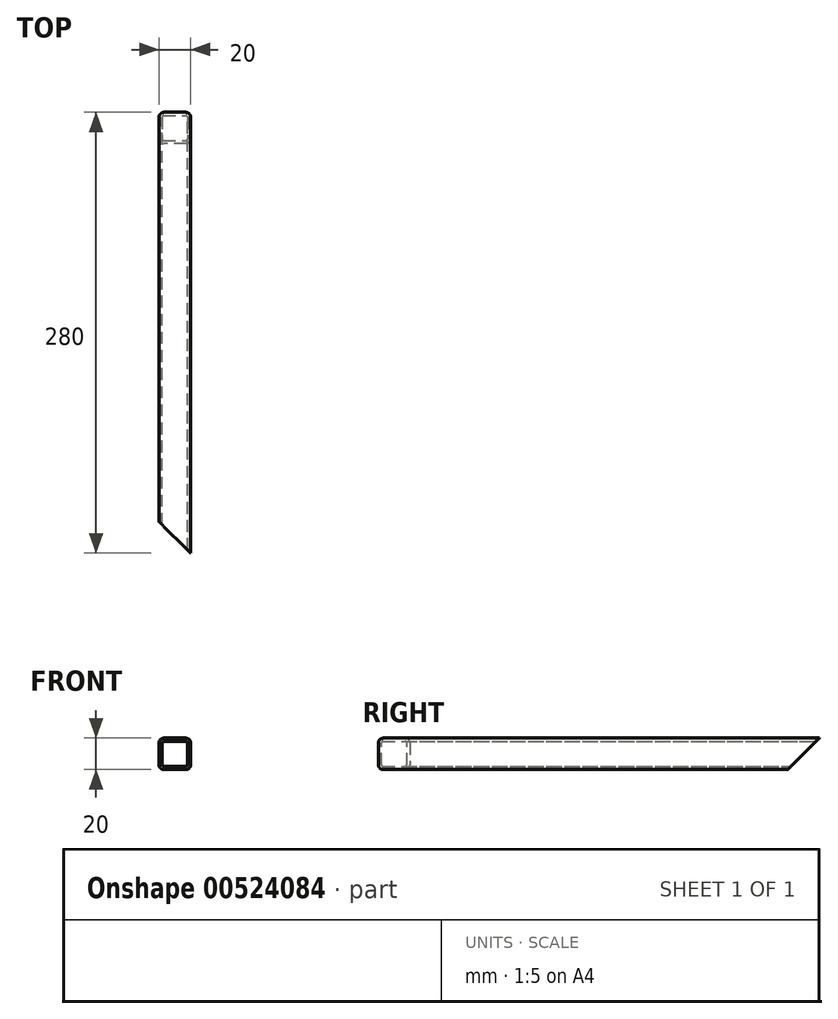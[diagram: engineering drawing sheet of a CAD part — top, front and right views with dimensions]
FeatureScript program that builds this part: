
annotation { "Feature Type Name" : "Feature", "Feature Type Description" : "" }
export const myFeature = defineFeature(function(context is Context, id is Id, definition is map)
    precondition{}
    {
        {
            assignVariable(context, id + "F0", {"name" : "R", "anyValue" : 3});
        }
        {
            assignVariable(context, id + "F1", {"name" : "W", "anyValue" : 2});
        }
        {
            var Q0;
            Q0=qCreatedBy(makeId("Front.planeOp"),FACE);
            var sketch = newSketch(context, id + "F2", { "sketchPlane" : qUnion([Q0])});
            skLineSegment(sketch, "E0.bottom", {"start": v(-10, 10) * mm, "end": v(10, 10) * mm});
            skLineSegment(sketch, "E0.top", {"start": v(-10, -10) * mm, "end": v(10, -10) * mm});
            skLineSegment(sketch, "E0.left", {"start": v(-10, 10) * mm, "end": v(-10, -10) * mm});
            skLineSegment(sketch, "E0.right", {"start": v(10, 10) * mm, "end": v(10, -10) * mm});
            skSolve(sketch);
        }
        {
            var Q0;
            Q0=qSketchRegion(id+"F2",true);
            extrude(context, id + "F3", {"entities" : qUnion([Q0]), "endBound" : BoundingType.SYMMETRIC, "depth" : 280 * mm, "offsetDistance" : 25 * mm});
        }
        {
            var Q0;
            Q0=makeQuery(id+"F3.opExtrude","SWEPT_EDGE",EDGE,{"disambiguationData":[OSD([sQuery(id+"F2.wireOp",EDGE,"E0.bottom"),sQuery(id+"F2.wireOp",EDGE,"E0.right")])]});
            var Q1;
            Q1=makeQuery(id+"F3.opExtrude","SWEPT_EDGE",EDGE,{"disambiguationData":[OSD([sQuery(id+"F2.wireOp",EDGE,"E0.bottom"),sQuery(id+"F2.wireOp",EDGE,"E0.left")])]});
            var Q2;
            Q2=makeQuery(id+"F3.opExtrude","SWEPT_EDGE",EDGE,{"disambiguationData":[OSD([sQuery(id+"F2.wireOp",EDGE,"E0.top"),sQuery(id+"F2.wireOp",EDGE,"E0.right")])]});
            var Q3;
            Q3=makeQuery(id+"F3.opExtrude","SWEPT_EDGE",EDGE,{"disambiguationData":[OSD([sQuery(id+"F2.wireOp",EDGE,"E0.top"),sQuery(id+"F2.wireOp",EDGE,"E0.left")])]});
            fillet(context, id + "F4", {"entities" : qUnion([Q0, Q1, Q2, Q3]), "radius" : (getVariable(context, 'R')) * mm, "tangentPropagation" : true, "allowEdgeOverflow" : false});
        }
        {
            var Q0;
            Q0=makeQuery(id+"F3.opExtrude","CAP_FACE",FACE,{"disambiguationData":[OSD([sQuery(id+"F2.wireOp",EDGE,"E0.bottom"),sQuery(id+"F2.wireOp",EDGE,"E0.top"),sQuery(id+"F2.wireOp",EDGE,"E0.left"),sQuery(id+"F2.wireOp",EDGE,"E0.right")])],"isStart":false});
            var Q1;
            Q1=makeQuery(id+"F3.opExtrude","CAP_FACE",FACE,{"disambiguationData":[OSD([sQuery(id+"F2.wireOp",EDGE,"E0.bottom"),sQuery(id+"F2.wireOp",EDGE,"E0.top"),sQuery(id+"F2.wireOp",EDGE,"E0.left"),sQuery(id+"F2.wireOp",EDGE,"E0.right")])],"isStart":true});
            shell(context, id + "F5", {"entities" : qUnion([Q0, Q1]), "thickness" : (getVariable(context, 'W')) * mm});
        }
        {
            var Q0;
            Q0=makeQuery(id+"F3.opExtrude","SWEPT_FACE",FACE,{"disambiguationData":[OSD([sQuery(id+"F2.wireOp",EDGE,"E0.left")])]});
            var sketch = newSketch(context, id + "F6", { "sketchPlane" : qUnion([Q0])});
            skLineSegment(sketch, "E1", {"start": v(-140, -10) * mm, "end": v(-120, -10) * mm});
            skLineSegment(sketch, "E2", {"start": v(-120, -10) * mm, "end": v(-140, 10) * mm});
            skLineSegment(sketch, "E3", {"start": v(-140, 10) * mm, "end": v(-140, -10) * mm});
            skSolve(sketch);
        }
        {
            var Q0;
            Q0=qSketchRegion(id+"F6",true);
            extrude(context, id + "F7", {"entities" : qUnion([Q0]), "operationType" : NewBodyOperationType.REMOVE, "endBound" : BoundingType.THROUGH_ALL, "oppositeDirection" : true, "depth" : 25 * mm, "offsetDistance" : 25 * mm});
        }
        {
            var Q0;
            Q0=makeQuery(id+"F3.opExtrude","SWEPT_FACE",FACE,{"disambiguationData":[OSD([sQuery(id+"F2.wireOp",EDGE,"E0.top")])]});
            var sketch = newSketch(context, id + "F8", { "sketchPlane" : qUnion([Q0])});
            skLineSegment(sketch, "E4.0", {"start": v(-10, 120) * mm, "end": v(-10, 140) * mm});
            skLineSegment(sketch, "E5", {"start": v(-10, 120) * mm, "end": v(10, 140) * mm});
            skLineSegment(sketch, "E6", {"start": v(10, 140) * mm, "end": v(-10, 140) * mm});
            skPoint(sketch, "E7.orphan", {"position": v(-10, -123) * mm});
            skPoint(sketch, "E8.0.end.orphan", {"position": v(10, -123) * mm});
            skSolve(sketch);
        }
        {
            var Q0;
            Q0 = qSketchRegion(id + "F8", true);
            extrude(context, id + "F9", {"entities" : qUnion([Q0]), "operationType" : NewBodyOperationType.REMOVE, "endBound" : BoundingType.THROUGH_ALL, "oppositeDirection" : true, "depth" : 25 * mm, "offsetDistance" : 25 * mm});
        }
    });
